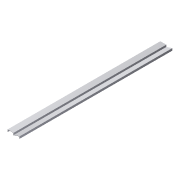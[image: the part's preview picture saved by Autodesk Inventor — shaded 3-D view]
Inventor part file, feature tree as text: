
AUTODESK INVENTOR PART (.ipt)
format: ipt  version: 2016 (Build 200138000, 138)  size: 85,504 bytes
history: native  units: mm
features: extrude x1, sketch x1
ambient origin geometry x8: Origin, YZ Plane, XZ Plane, XY Plane, X Axis, Y Axis, Z Axis, Center Point
bodies: Solid1 (feature_tree)
feature tree (2):
  extrude  "Extrusion1"  Depth=10.0mm
  sketch  "Sketch1"  dims[d0=56.0mm d1=10.0mm d2=9.0mm d3=26.0mm d4=9.0mm d5=711.2mm d6=0.0mm]
